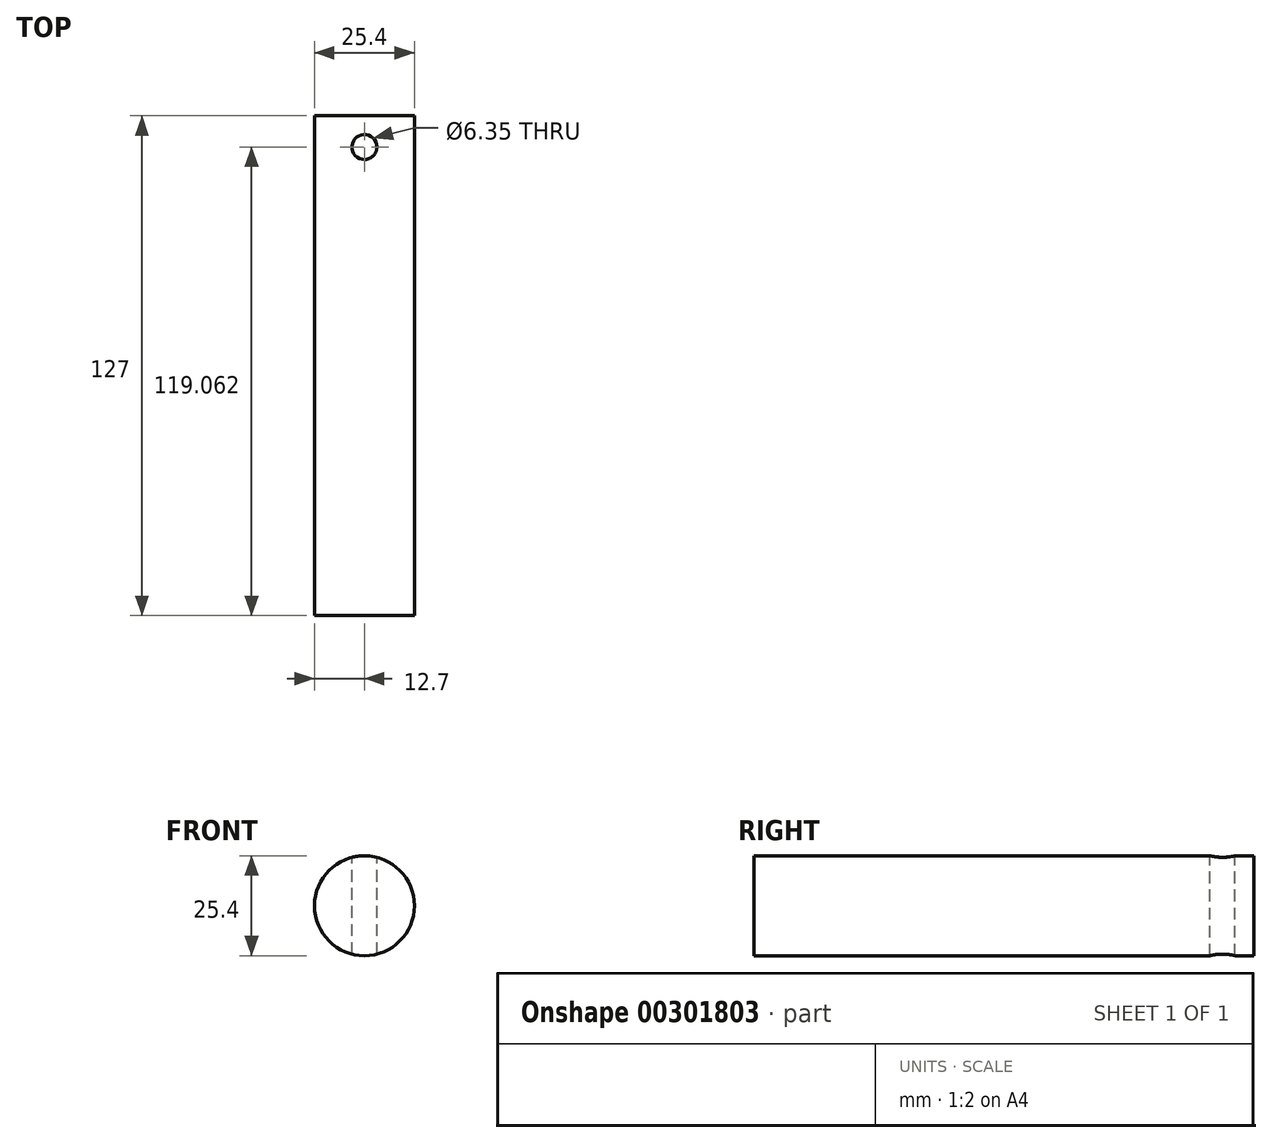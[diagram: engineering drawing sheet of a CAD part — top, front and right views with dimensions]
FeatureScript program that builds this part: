
annotation { "Feature Type Name" : "Feature", "Feature Type Description" : "" }
export const myFeature = defineFeature(function(context is Context, id is Id, definition is map)
    precondition{}
    {
        {
            var Q0;
            Q0=qCreatedBy(makeId("Front.planeOp"),FACE);
            var sketch = newSketch(context, id + "F0", { "sketchPlane" : qUnion([Q0])});
            skCircle(sketch, "E0", {"center": v(0, 0) * mm, "radius": 12.7 * mm});
            skSolve(sketch);
        }
        {
            var Q0;
            Q0=makeQuery(id+"F0.imprint","IMPRINT",FACE,{"disambiguationData":[TD([[makeQuery(id+"F0.imprint","IMPRINT",EDGE,{"derivedFrom":sQuery(id+"F0.wireOp",EDGE,"E0")}),1.0]])]});
            extrude(context, id + "F1", {"entities" : qUnion([Q0]), "depth" : 127 * mm});
        }
        {
            var Q0;
            Q0=qCreatedBy(makeId("Top.planeOp"),FACE);
            cPlane(context, id + "F2", {"entities" : qUnion([Q0]), "cplaneType" : CPlaneType.OFFSET, "offset" : 12.7 * mm, "width" : 152.4 * mm, "height" : 152.4 * mm});
        }
        {
            var Q0;
            Q0=qCreatedBy(id+"F2.planeOp",FACE);
            var sketch = newSketch(context, id + "F3", { "sketchPlane" : qUnion([Q0])});
            skCircle(sketch, "E1", {"center": v(0, -7.94) * mm, "radius": 3.18 * mm});
            skSolve(sketch);
        }
        {
            var Q0;
            Q0=makeQuery(id+"F3.imprint","IMPRINT",FACE,{"disambiguationData":[TD([[makeQuery(id+"F3.imprint","IMPRINT",EDGE,{"derivedFrom":sQuery(id+"F3.wireOp",EDGE,"E1")}),1.0]])]});
            extrude(context, id + "F4", {"entities" : qUnion([Q0]), "operationType" : NewBodyOperationType.REMOVE, "endBound" : BoundingType.THROUGH_ALL, "oppositeDirection" : true, "depth" : 25.4 * mm});
        }
    });
